# Revit family: Faucet-Single_Handle-American Standard-Colony Pro-7077300_Series
name_source: partatom
category: Plumbing Fixtures
units: mm (PartAtom-declared; Revit-internal decimal feet)

## family parameters
Always vertical = No
Cut with Voids When Loaded = No
OmniClass Number = 23.45.55.14
OmniClass Title = Single Faucets
Part Type = Normal
Room Calculation Point = No
Round Connector Dimension = Use Diameter
Shared = Yes
Work Plane-Based = Yes

## types (3) — shared parameters
ADA Compliant = Yes
Assembly Code = D2020300
CEC Compliant = Yes
CW Connection = No
CWFU = 1.5
CalGreen Compliant = Yes
Default Elevation = 0"
Description = Colony® PRO Single-Handle Pull-Down Dual Spray Kitchen Faucet 1.5 gpm/5.7 L/min
Flow Rate = 1.5 gpm/5.7 L/min
HW Connection = No
HWFU = 1.5
IAPMO Compliance = ANSI A117.1, ASME A112.18.1, CSA B125.1, NSF/ANSI/CAN 61: Q<1, NSF/ANSI/CAN 372
Installation Instruction Link = https://lixil.cdn.celum.cloud
Installation Type = Deck Mounted
Length = 8 11/16"
Manufacturer = American Standard
Product Documentation Link = https://lixil.cdn.celum.cloud
Product Page URL = https://www.americanstandard-us.com
Tempered Water Connection = Yes
Tempered Water Connection Diameter = 3/8"
URL = http://www.americanstandard-us.com
Vent Connection = No
Warranty Information = Limited lifetime warranty
Waste Connection = No
Width = 10 11/16"

## per-type parameters (varying)
| type | Deck Plate | Finish | Height | Material | Mounting Height Faucet | WFU |
| 7077300.002 | Yes | Brass-American Standard-002-Polished Chrome | 16 13/16" | Brass-American Standard-002-Polished Chrome | 3/8" | 0 |
| 7077300.075 | Yes | Brass-American Standard-075-Stainless Steel | 16 13/16" | Brass-American Standard-075-Stainless Steel | 3/8" | 0 |
| 7077300.243 | No | Brass-American Standard-243-Matte Black | 16 7/16" | Brass-American Standard-243-Matte Black | 0" | 2 |

note: column(s) folded — value = type name in every type: Model

## geometry (parser evidence)
native form markers: Sweep x4
no freeform markers — native parametric forms only
